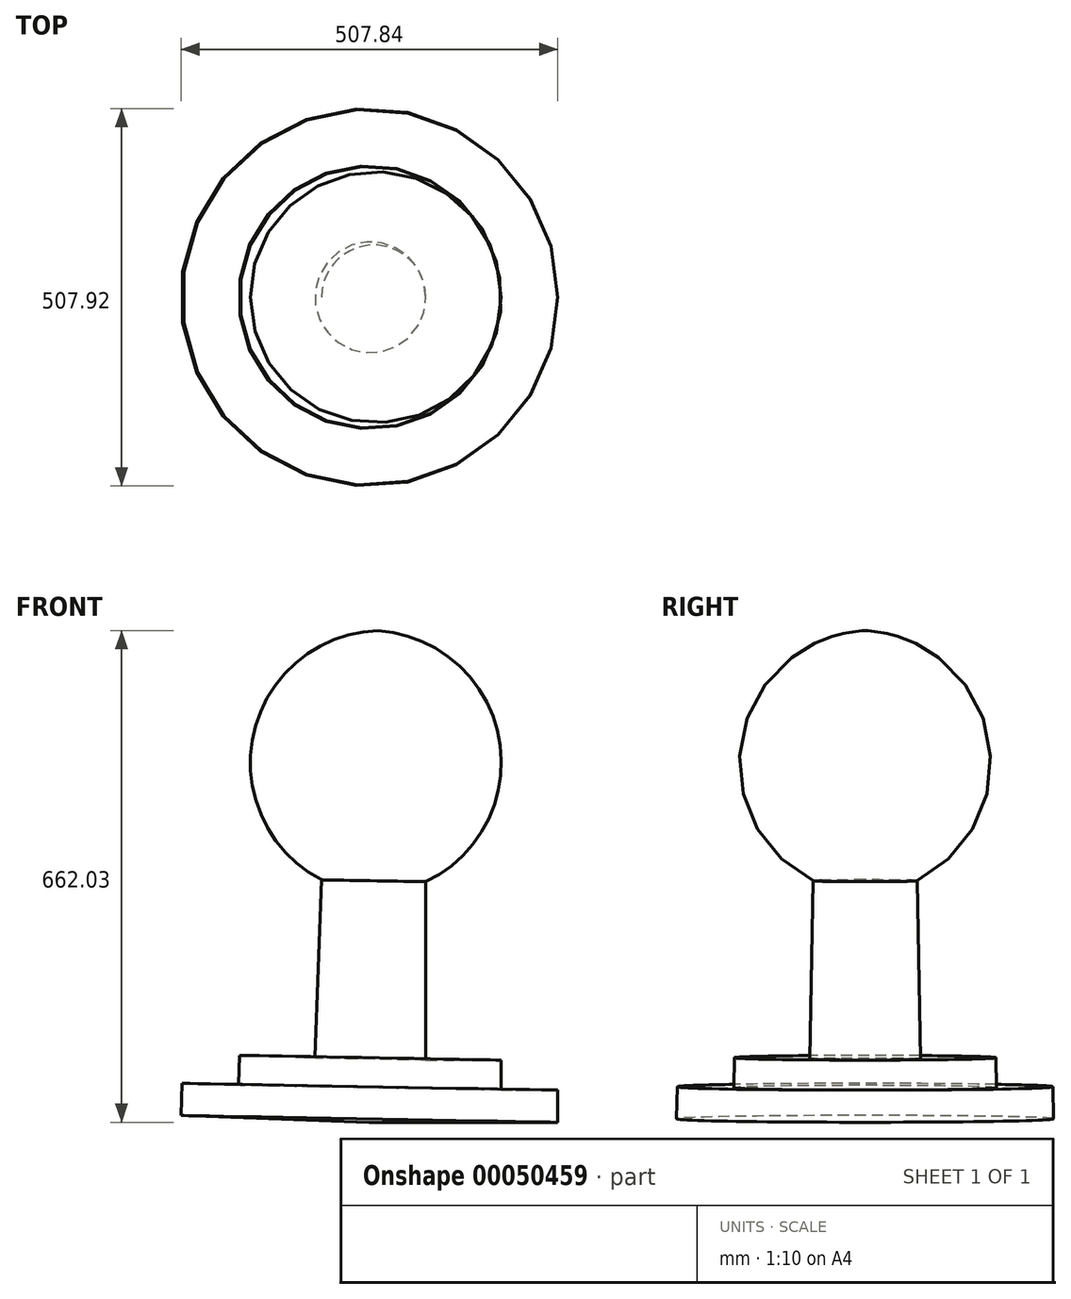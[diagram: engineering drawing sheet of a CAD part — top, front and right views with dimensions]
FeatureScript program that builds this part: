
annotation { "Feature Type Name" : "Feature", "Feature Type Description" : "" }
export const myFeature = defineFeature(function(context is Context, id is Id, definition is map)
    precondition{}
    {
        {
            var Q0;
            Q0=qCreatedBy(makeId("Front.planeOp"),FACE);
            var sketch = newSketch(context, id + "F0", { "sketchPlane" : qUnion([Q0])});
            skLineSegment(sketch, "E0", {"start": v(0, 0) * mm, "end": v(254, 0) * mm});
            skLineSegment(sketch, "E1", {"start": v(254, 0) * mm, "end": v(254, 43.25) * mm});
            skLineSegment(sketch, "E2", {"start": v(254, 43.25) * mm, "end": v(177.8, 43.25) * mm});
            skLineSegment(sketch, "E3", {"start": v(177.8, 43.25) * mm, "end": v(177.8, 83.75) * mm});
            skLineSegment(sketch, "E4", {"start": v(177.8, 83.75) * mm, "end": v(76.2, 83.75) * mm});
            skLineSegment(sketch, "E5", {"start": v(76.2, 83.75) * mm, "end": v(76.2, 323.98) * mm});
            skArc(sketch, "E6", {"start": v(76.2, 323.98) * mm, "mid": v(174.67, 517.84) * mm, "end": v(11.9, 662.03) * mm});
            skLineSegment(sketch, "E7", {"start": v(5.67, 315.13) * mm, "end": v(16, 889.95) * mm, "construction": true});
            skPoint(sketch, "E8.end.orphan", {"position": v(0, 328.54) * mm});
            skLineSegment(sketch, "E9", {"start": v(11.9, 662.03) * mm, "end": v(0, 0) * mm});
            skLineSegment(sketch, "E10", {"start": v(13.31, 740.1) * mm, "end": v(-2.27, -126.06) * mm});
            skSolve(sketch);
        }
        {
            var Q0;
            {var subQ0=sQuery(id+"F0.wireOp",EDGE,"E0");Q0=makeQuery(id+"F0.imprint","IMPRINT",FACE,{"disambiguationData":[TD([[makeQuery(id+"F0.imprint","IMPRINT",EDGE,{"derivedFrom":subQ0}),1.0]])]});}
            var Q1;
            Q1=sQuery(id+"F0.wireOp",EDGE,"E10");
            revolve(context, id + "F1", {"entities" : qUnion([Q0]), "axis" : qUnion([Q1]), "revolveType" : RevolveType.FULL});
        }
    });
